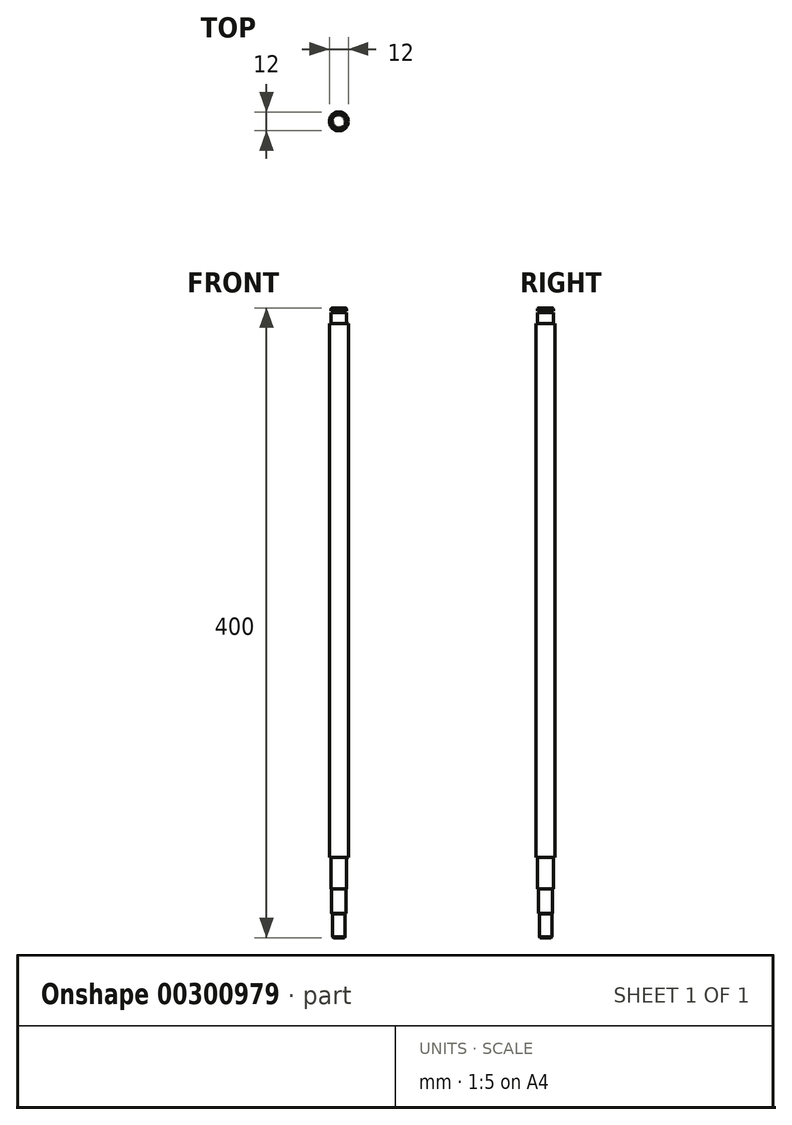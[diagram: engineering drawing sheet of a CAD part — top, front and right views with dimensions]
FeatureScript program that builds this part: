
annotation { "Feature Type Name" : "Feature", "Feature Type Description" : "" }
export const myFeature = defineFeature(function(context is Context, id is Id, definition is map)
    precondition{}
    {
        {
            var Q0;
            Q0=qCreatedBy(makeId("Front.planeOp"),FACE);
            var sketch = newSketch(context, id + "F0", { "sketchPlane" : qUnion([Q0])});
            skLineSegment(sketch, "E0", {"start": v(0, 0) * mm, "end": v(0, 285.84) * mm, "construction": true});
            skLineSegment(sketch, "E1", {"start": v(0, 0) * mm, "end": v(3.5, 0) * mm});
            skLineSegment(sketch, "E2", {"start": v(3.5, 0) * mm, "end": v(4, 0.5) * mm});
            skLineSegment(sketch, "E3", {"start": v(4, 0.5) * mm, "end": v(4, 15) * mm});
            skLineSegment(sketch, "E4", {"start": v(4, 15) * mm, "end": v(4.5, 15.5) * mm});
            skLineSegment(sketch, "E5", {"start": v(4.5, 15.5) * mm, "end": v(4.5, 31) * mm});
            skLineSegment(sketch, "E6", {"start": v(4.5, 31) * mm, "end": v(5, 31) * mm});
            skLineSegment(sketch, "E7", {"start": v(5, 31) * mm, "end": v(5, 51) * mm});
            skLineSegment(sketch, "E8", {"start": v(5, 51) * mm, "end": v(6, 51) * mm});
            skLineSegment(sketch, "E9", {"start": v(6, 51) * mm, "end": v(6, 390) * mm});
            skLineSegment(sketch, "E10", {"start": v(6, 390) * mm, "end": v(5, 390) * mm});
            skLineSegment(sketch, "E11", {"start": v(5, 390) * mm, "end": v(5, 397) * mm});
            skLineSegment(sketch, "E12", {"start": v(5, 397) * mm, "end": v(3.8, 397) * mm});
            skLineSegment(sketch, "E13", {"start": v(3.8, 397) * mm, "end": v(3.8, 397.9) * mm});
            skLineSegment(sketch, "E14", {"start": v(3.8, 397.9) * mm, "end": v(5, 397.9) * mm});
            skLineSegment(sketch, "E15", {"start": v(5, 397.9) * mm, "end": v(5, 399.5) * mm});
            skLineSegment(sketch, "E16", {"start": v(5, 399.5) * mm, "end": v(4.5, 400) * mm});
            skLineSegment(sketch, "E17", {"start": v(4.5, 400) * mm, "end": v(0, 400) * mm});
            skLineSegment(sketch, "E18", {"start": v(0, 400) * mm, "end": v(0, 0) * mm});
            skSolve(sketch);
        }
        {
            var Q0;
            Q0 = qSketchRegion(id + "F0", true);
            var Q1;
            Q1=sQuery(id+"F0.wireOp",EDGE,"E0");
            revolve(context, id + "F1", {"entities" : qUnion([Q0]), "axis" : qUnion([Q1]), "revolveType" : RevolveType.FULL});
        }
    });
